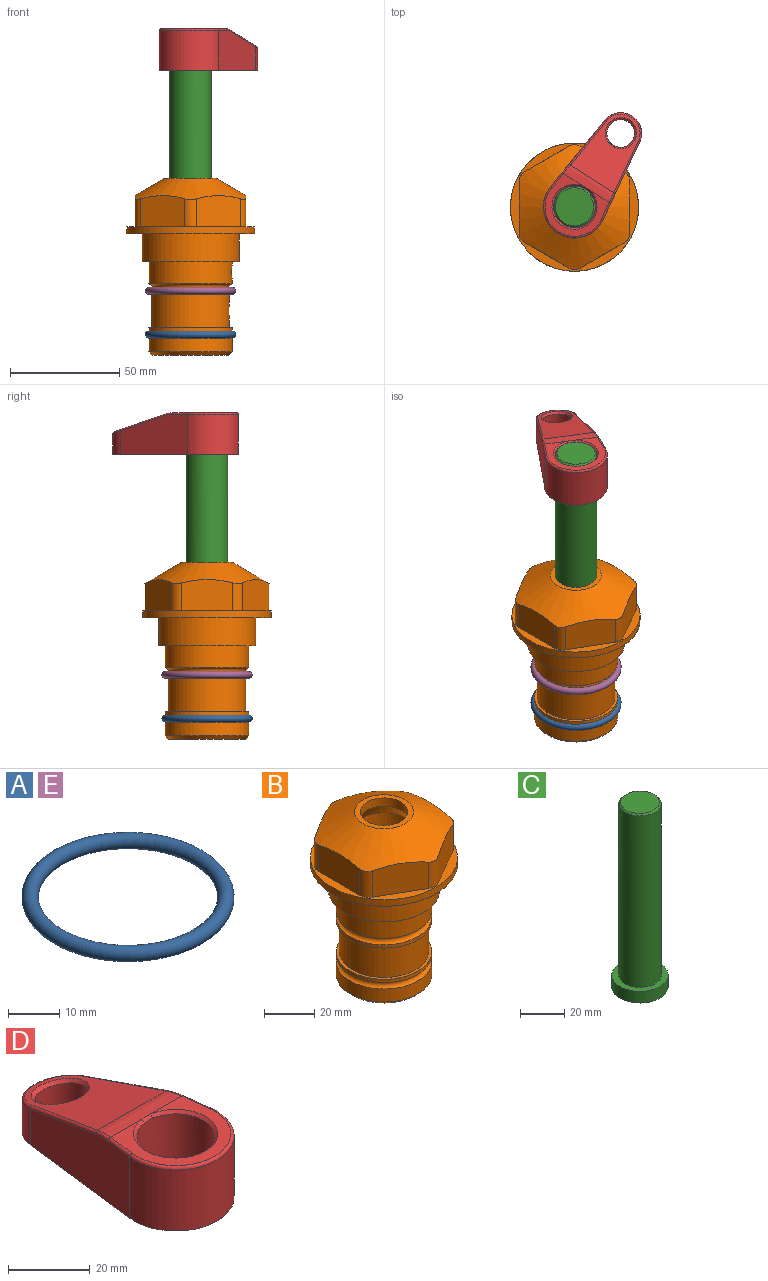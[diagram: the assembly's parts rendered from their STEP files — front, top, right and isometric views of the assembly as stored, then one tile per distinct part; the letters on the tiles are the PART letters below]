
ASSEMBLY  parts=5 mates=4
PART A: 1 faces, bbox 44.7x44.7x3.2 mm
  f0: torus R=19.05mm, axis (0,0,1), area 1193.9mm2
PART B: 36 faces, bbox 58.7x58.7x81 mm
  f0: cylinder r=17.78mm len=35.56mm, axis (0,0,1), area 1670.8mm2, adj f23,f24,f31
  f1: cylinder r=19.05mm len=38.1mm, axis (0,0,1), area 1191.9mm2, adj f26,f27,f30
  f2: plane 58.66x58.66mm, normal (0,0,-1), area 1150.6mm2, adj f3,f28
  f3: cylinder r=29.33mm len=58.66mm, axis (0,0,-1), area 585.1mm2, adj f2,f4
  f4: plane 58.66x58.66mm, normal (0,0,1), area 475.9mm2, adj f3,f5,f6,f7,f8,f9,f10,f11
  f5: plane 20.32x14.34mm, normal (-0.5,0.87,0), area 324.4mm2, adj f4,f15,f16,f17
  f6: plane 20.32x14.34mm, normal (0.5,0.87,0), area 324.4mm2, adj f4,f14,f15,f17
  f7: plane 23.48x14.34mm, normal (1,0,0), area 324.4mm2, adj f4,f13,f14,f17
  f8: plane 20.32x14.34mm, normal (0.5,-0.87,0), area 324.4mm2, adj f4,f12,f13,f17
  f9: plane 20.32x14.34mm, normal (-0.5,-0.87,0), area 324.4mm2, adj f4,f11,f12,f17
  f10: plane 23.48x14.34mm, normal (-1,0,0), area 324.4mm2, adj f4,f11,f16,f17
  f11: cylinder r=5.08mm len=12.85mm, axis (0,0,-1), area 67.2mm2, adj f4,f9,f10,f17
  f12: cylinder r=5.08mm len=12.85mm, axis (0,0,-1), area 67.2mm2, adj f4,f8,f9,f17
  f13: cylinder r=5.08mm len=12.85mm, axis (0,0,-1), area 67.2mm2, adj f4,f7,f8,f17
  f14: cylinder r=5.08mm len=12.85mm, axis (0,0,-1), area 67.2mm2, adj f4,f6,f7,f17
  f15: cylinder r=5.08mm len=12.85mm, axis (0,0,-1), area 67.2mm2, adj f4,f5,f6,f17
  f16: cylinder r=5.08mm len=12.85mm, axis (0,0,-1), area 67.2mm2, adj f4,f5,f10,f17
  f17: cone r=11.73mm half-angle=60deg, axis (0,0,-1), area 2071.8mm2, adj f5,f6,f7,f8,f9,f10,f11,f12
  f18: plane 23.46x23.46mm, normal (0,0,1), area 147.4mm2, adj f17,f35
  f19: plane 34.93x34.93mm, normal (0,0,-1), area 958mm2, adj f29
  f20: cylinder r=19.05mm len=38.1mm, axis (0,0,1), area 760.1mm2, adj f21,f29
  f21: torus R=19.05mm, axis (0,0,1), area 565.3mm2, adj f20,f22
  f22: cylinder r=19.05mm len=38.1mm, axis (0,0,1), area 190mm2, adj f21,f23
  f23: plane 38.1x38.1mm, normal (0,0,1), area 146.9mm2, adj f0,f22
  f24: plane 38.1x38.1mm, normal (0,0,-1), area 146.9mm2, adj f0,f25
  f25: cylinder r=19.05mm len=38.1mm, axis (0,0,1), area 190mm2, adj f24,f26
  f26: torus R=19.05mm, axis (0,0,1), area 565.3mm2, adj f1,f25
  f27: plane 44.45x44.45mm, normal (0,0,-1), area 411.7mm2, adj f1,f28
  f28: cylinder r=22.23mm len=44.45mm, axis (0,0,1), area 1773.5mm2, adj f2,f27
  f29: cone r=19.05mm half-angle=45deg, axis (0,0,1), area 257.5mm2, adj f19,f20
  f30: cylinder r=3.17mm len=6.75mm, axis (-1,0,0), area 128mm2, adj f1,f33
  f31: cylinder r=3.17mm len=6.35mm, axis (-1,0,0), area 102.5mm2, adj f0,f33
  f32: plane 25.4x25.4mm, normal (0,0,1), area 506.7mm2, adj f33
  f33: cylinder r=12.7mm len=66.42mm, axis (0,0,-1), area 5236.2mm2, adj f30,f31,f32,f34
  f34: cone r=9.53mm half-angle=30deg, axis (0,0,-1), area 443.4mm2, adj f33,f35
  f35: cylinder r=9.53mm len=19.05mm, axis (0,0,-1), area 240.9mm2, adj f18,f34
PART C: 6 faces, bbox 25.4x25.4x101.6 mm
  f0: plane 17.46x17.46mm, normal (0,0,1), area 239.5mm2, adj f5
  f1: plane 25.4x25.4mm, normal (0,0,-1), area 506.7mm2, adj f2
  f2: cylinder r=12.7mm len=25.4mm, axis (0,0,1), area 506.7mm2, adj f1,f3
  f3: plane 25.4x25.4mm, normal (0,0,1), area 221.7mm2, adj f2,f4
  f4: cylinder r=9.53mm len=94.46mm, axis (0,0,1), area 5653mm2, adj f3,f5
  f5: cone r=8.73mm half-angle=45deg, axis (0,0,-1), area 64.4mm2, adj f0,f4
PART D: 31 faces, bbox 31.7x65.5x19.8 mm
  f0: plane 39.12x18.26mm, normal (0.99,0.12,0), area 612.2mm2, adj f1,f4,f7,f11,f13,f15
  f1: cylinder r=9.53mm len=18.91mm, axis (0,0,-1), area 296.1mm2, adj f0,f2,f7,f17
  f2: plane 39.12x18.26mm, normal (-0.99,0.12,0), area 612.2mm2, adj f1,f4,f7,f12,f14,f16
  f3: cylinder r=6.35mm len=12.7mm, axis (0,0,-1), area 362.4mm2, adj f7,f18
  f4: cylinder r=14.29mm len=28.58mm, axis (0,0,-1), area 882.2mm2, adj f0,f2,f7,f10
  f5: cylinder r=9.53mm len=19.05mm, axis (0,0,-1), area 1092.6mm2, adj f7,f19,f20
  f6: plane 26.99x23.69mm, normal (0,0,1), area 216.2mm2, adj f9,f10,f11,f12,f19
  f7: plane 63.5x28.58mm, normal (0,0,-1), area 661.8mm2, adj f0,f1,f2,f3,f4,f5,f22,f23
  f8: plane 33.52x23.6mm, normal (0,0.26,0.97), area 486mm2, adj f9,f15,f16,f17,f18
  f9: cylinder r=19.05mm len=24.72mm, axis (1,0,0), area 120.4mm2, adj f6,f8,f13,f14,f20
  f10: torus R=13.49mm, axis (0,0,1), area 59mm2, adj f4,f6,f11,f12
  f11: cylinder r=0.79mm len=8.67mm, axis (0.12,-0.99,0), area 10.8mm2, adj f0,f6,f10,f13
  f12: cylinder r=0.79mm len=8.67mm, axis (0.12,0.99,0), area 10.8mm2, adj f2,f6,f10,f14
  f13: bspline ~4.95x1.42mm, area 6.1mm2, adj f0,f9,f11,f15
  f14: bspline ~4.95x1.42mm, area 6.1mm2, adj f2,f9,f12,f16
  f15: cylinder r=0.79mm len=25.95mm, axis (0.12,-0.96,0.26), area 32.9mm2, adj f0,f8,f13,f17
  f16: cylinder r=0.79mm len=25.95mm, axis (0.12,0.96,-0.26), area 32.9mm2, adj f2,f8,f14,f17
  f17: bspline ~18.91x8.38mm, area 30mm2, adj f1,f8,f15,f16
  f18: bspline ~14.29x14.29mm, area 48.3mm2, adj f3,f8
  f19: cone r=9.53mm half-angle=45deg, axis (0,0,1), area 66.5mm2, adj f5,f6,f20
  f20: bspline ~3.22x0.96mm, area 3.5mm2, adj f5,f9,f19
  f21: plane 2.75x2.72mm, normal (0,0,-1), area 2.9mm2, adj f23,f25,f28
  f22: plane 23.05x15.88mm, normal (-0.99,-0.12,0), area 323.6mm2, adj f7,f25,f26,f27,f28,f29
  f23: plane 23.05x15.88mm, normal (0.99,-0.12,0), area 323.6mm2, adj f7,f21,f25,f27,f28,f30
  f24: cylinder r=9.53mm len=10.69mm, axis (0,0,-1), area 114.7mm2, adj f7,f27,f29,f30
  f25: cylinder r=12.7mm len=20.59mm, axis (0,0,-1), area 381.1mm2, adj f7,f21,f22,f23,f26,f28
  f26: plane 2.75x2.72mm, normal (0,0,-1), area 2.9mm2, adj f22,f25,f28
  f27: plane 19.72x18.37mm, normal (0,-0.26,-0.97), area 291.8mm2, adj f22,f23,f24,f28,f29,f30
  f28: cylinder r=15.88mm len=19.92mm, axis (1,0,0), area 54.8mm2, adj f21,f22,f23,f25,f26,f27
  f29: cylinder r=1.59mm len=11mm, axis (0,0,-1), area 34.7mm2, adj f7,f22,f24,f27
  f30: cylinder r=1.59mm len=11mm, axis (0,0,-1), area 34.7mm2, adj f7,f23,f24,f27
PART E: same geometry as A
PLACE A t=(0,0,-21.59)mm
PLACE B at identity fixed
PLACE C rot(axis=(0,0,-1),32.2deg) t=(0,0,30.41)mm
PLACE D rot(axis=(0,0,-1),32.2deg) t=(0,0,30.41)mm
PLACE E t=(0,0,-1.59)mm
MATE fastened C.f2 <-> D.f4  axis (0,0,1) through (0,0,93.91)mm
MATE fastened A.f0 <-> B.f0  axis (0,0,1) through (0,0,-46.1)mm
MATE cylindrical C.f2 <-> B.f0  axis (0,0,-1) through (0,0,-7.69)mm
MATE fastened E.f0 <-> B.f0  axis (0,0,1) through (0,0,-26.1)mm
